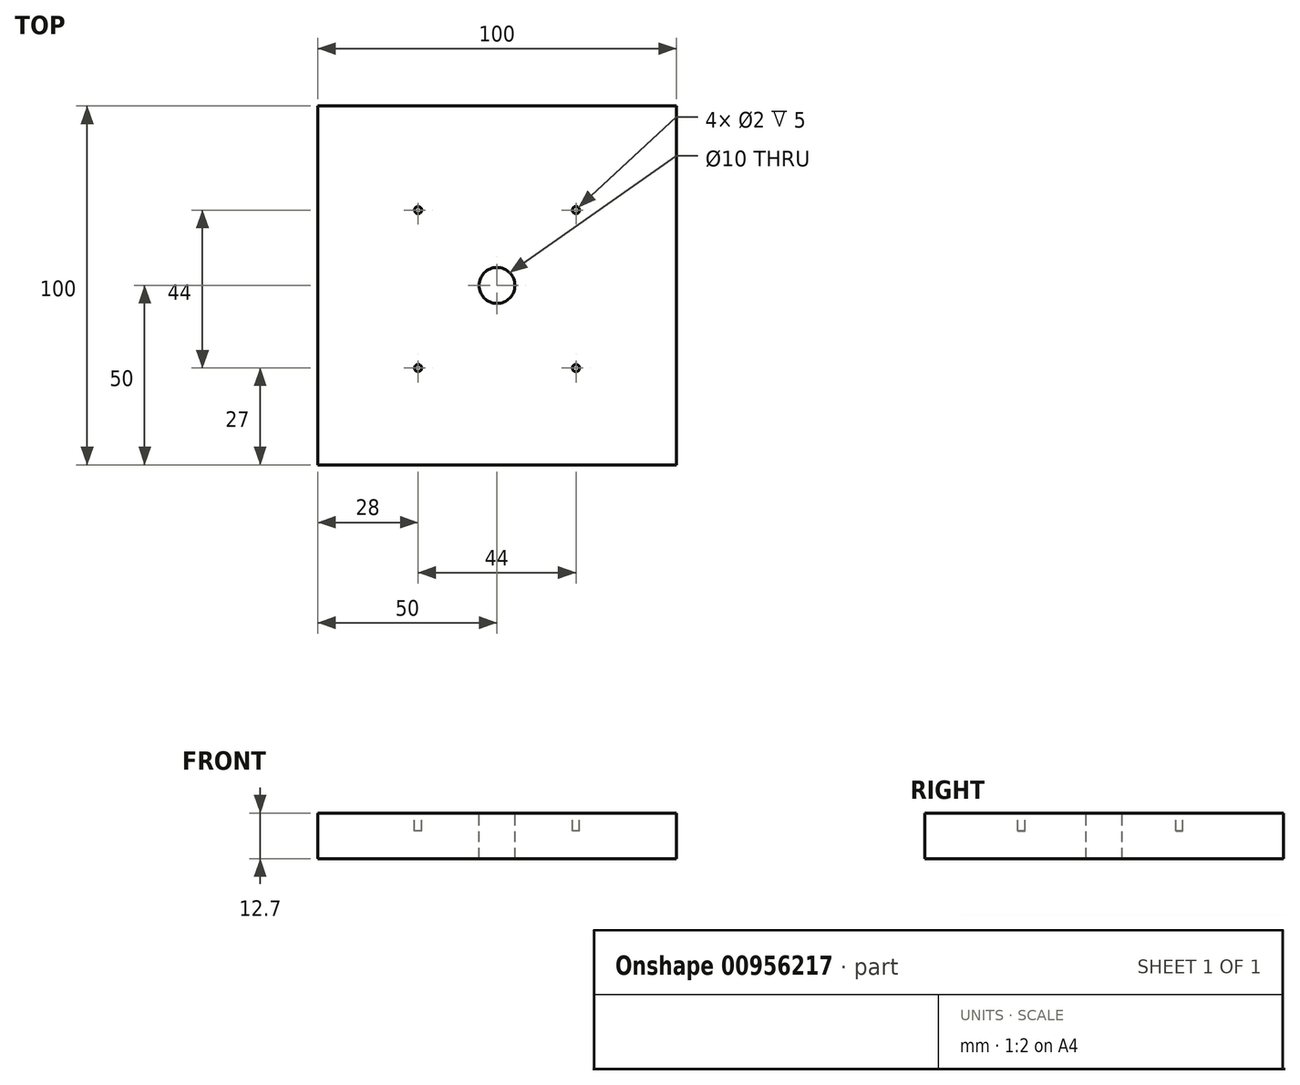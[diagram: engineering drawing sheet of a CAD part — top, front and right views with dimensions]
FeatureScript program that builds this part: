
annotation { "Feature Type Name" : "Feature", "Feature Type Description" : "" }
export const myFeature = defineFeature(function(context is Context, id is Id, definition is map)
    precondition{}
    {
        {
            var Q0;
            Q0=qCreatedBy(makeId("Top.planeOp"),FACE);
            var sketch = newSketch(context, id + "F0", { "sketchPlane" : qUnion([Q0])});
            skLineSegment(sketch, "E0.bottom", {"start": v(50, 50) * mm, "end": v(-50, 50) * mm});
            skLineSegment(sketch, "E0.top", {"start": v(50, -50) * mm, "end": v(-50, -50) * mm});
            skLineSegment(sketch, "E0.left", {"start": v(50, 50) * mm, "end": v(50, -50) * mm});
            skLineSegment(sketch, "E0.right", {"start": v(-50, 50) * mm, "end": v(-50, -50) * mm});
            skPoint(sketch, "E0.middle", {"position": v(0, 0) * mm});
            skSolve(sketch);
        }
        {
            var Q0;
            Q0=makeQuery(id+"F0.imprint","IMPRINT",FACE,{"disambiguationData":[TD([[makeQuery(id+"F0.imprint","IMPRINT",EDGE,{"derivedFrom":sQuery(id+"F0.wireOp",EDGE,"E0.bottom")}),1.0]])]});
            extrude(context, id + "F1", {"entities" : qUnion([Q0]), "depth" : 12.7 * mm, "offsetDistance" : 25 * mm});
        }
        {
            var Q0;
            Q0=makeQuery(id+"F1.opExtrude","CAP_FACE",FACE,{"disambiguationData":[OSD([sQuery(id+"F0.wireOp",EDGE,"E0.bottom"),sQuery(id+"F0.wireOp",EDGE,"E0.top"),sQuery(id+"F0.wireOp",EDGE,"E0.left"),sQuery(id+"F0.wireOp",EDGE,"E0.right")])],"isStart":false});
            var sketch = newSketch(context, id + "F2", { "sketchPlane" : qUnion([Q0])});
            skCircle(sketch, "E1", {"center": v(0, 0) * mm, "radius": 5 * mm});
            skCircle(sketch, "E2", {"center": v(-22, 21) * mm, "radius": 1 * mm});
            skCircle(sketch, "E3.0.1.0", {"center": v(-22, -23) * mm, "radius": 1 * mm});
            skCircle(sketch, "E3.1.0.0", {"center": v(22, 21) * mm, "radius": 1 * mm});
            skCircle(sketch, "E3.1.1.0", {"center": v(22, -23) * mm, "radius": 1 * mm});
            skLineSegment(sketch, "E3.direction1", {"start": v(-22, 21) * mm, "end": v(22, 21) * mm, "construction": true});
            skLineSegment(sketch, "E3.direction2", {"start": v(-22, 21) * mm, "end": v(-22, -23) * mm, "construction": true});
            skSolve(sketch);
        }
        {
            var Q0;
            Q0=makeQuery(id+"F2.imprint","IMPRINT",FACE,{"disambiguationData":[TD([[makeQuery(id+"F2.imprint","IMPRINT",EDGE,{"derivedFrom":sQuery(id+"F2.wireOp",EDGE,"E1")}),1.0]])]});
            extrude(context, id + "F3", {"entities" : qUnion([Q0]), "operationType" : NewBodyOperationType.REMOVE, "oppositeDirection" : true, "depth" : 25 * mm, "offsetDistance" : 25 * mm});
        }
        {
            var Q0;
            Q0=makeQuery(id+"F2.imprint","IMPRINT",FACE,{"disambiguationData":[TD([[makeQuery(id+"F2.imprint","IMPRINT",EDGE,{"derivedFrom":sQuery(id+"F2.wireOp",EDGE,"E2")}),1.0]])]});
            var Q1;
            Q1=makeQuery(id+"F2.imprint","IMPRINT",FACE,{"disambiguationData":[TD([[makeQuery(id+"F2.imprint","IMPRINT",EDGE,{"derivedFrom":sQuery(id+"F2.wireOp",EDGE,"E3.1.0.0")}),1.0]])]});
            var Q2;
            Q2=makeQuery(id+"F2.imprint","IMPRINT",FACE,{"disambiguationData":[TD([[makeQuery(id+"F2.imprint","IMPRINT",EDGE,{"derivedFrom":sQuery(id+"F2.wireOp",EDGE,"E3.1.1.0")}),1.0]])]});
            var Q3;
            Q3=makeQuery(id+"F2.imprint","IMPRINT",FACE,{"disambiguationData":[TD([[makeQuery(id+"F2.imprint","IMPRINT",EDGE,{"derivedFrom":sQuery(id+"F2.wireOp",EDGE,"E3.0.1.0")}),1.0]])]});
            extrude(context, id + "F4", {"entities" : qUnion([Q0, Q1, Q2, Q3]), "operationType" : NewBodyOperationType.REMOVE, "oppositeDirection" : true, "depth" : 5 * mm, "offsetDistance" : 25 * mm});
        }
    });
